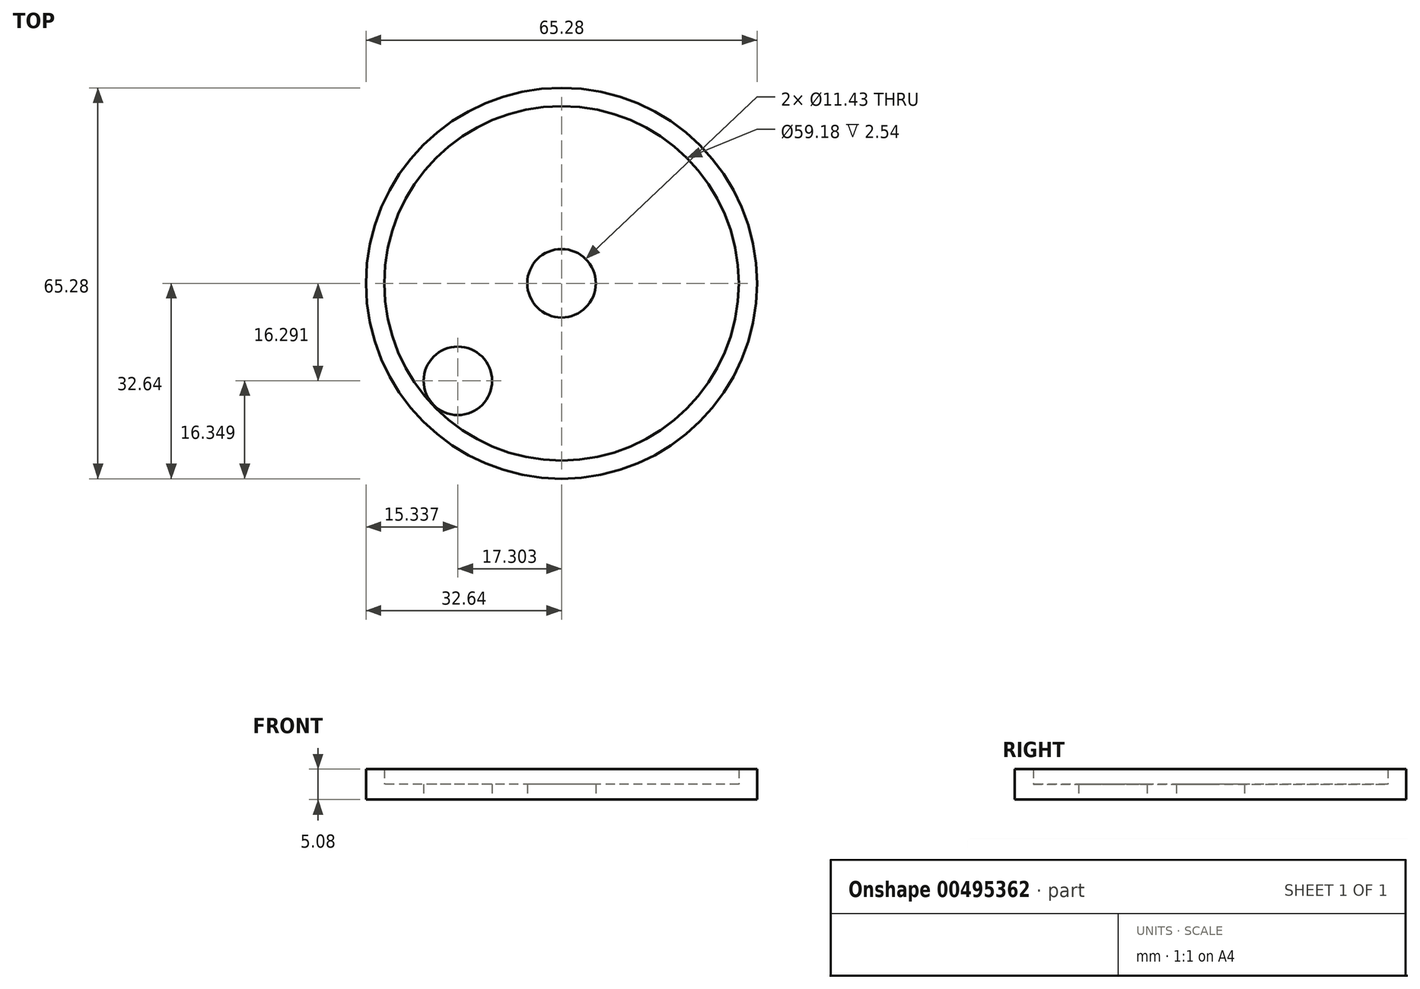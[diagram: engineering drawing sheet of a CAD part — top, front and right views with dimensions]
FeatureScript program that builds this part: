
annotation { "Feature Type Name" : "Feature", "Feature Type Description" : "" }
export const myFeature = defineFeature(function(context is Context, id is Id, definition is map)
    precondition{}
    {
        {
            var Q0;
            Q0=qCreatedBy(makeId("Top.planeOp"),FACE);
            var sketch = newSketch(context, id + "F0", { "sketchPlane" : qUnion([Q0])});
            skCircle(sketch, "E0", {"center": v(0, 0) * mm, "radius": 32.64 * mm});
            skCircle(sketch, "E1", {"center": v(0, 0) * mm, "radius": 29.6 * mm});
            skCircle(sketch, "E2", {"center": v(0, 0) * mm, "radius": 5.72 * mm});
            skCircle(sketch, "E3", {"center": v(-17.3, -16.3) * mm, "radius": 5.72 * mm});
            skSolve(sketch);
        }
        {
            var Q0;
            Q0=makeQuery(id+"F0.imprint","IMPRINT",FACE,{"disambiguationData":[TD([[makeQuery(id+"F0.imprint","IMPRINT",EDGE,{"derivedFrom":sQuery(id+"F0.wireOp",EDGE,"E0")}),1.0]])]});
            extrude(context, id + "F1", {"entities" : qUnion([Q0]), "depth" : 5.08 * mm});
        }
        {
            var Q0;
            Q0=makeQuery(id+"F0.imprint","IMPRINT",FACE,{"disambiguationData":[TD([[makeQuery(id+"F0.imprint","IMPRINT",EDGE,{"derivedFrom":sQuery(id+"F0.wireOp",EDGE,"E1")}),1.0]])]});
            extrude(context, id + "F2", {"entities" : qUnion([Q0]), "operationType" : NewBodyOperationType.ADD, "depth" : 2.54 * mm});
        }
    });
